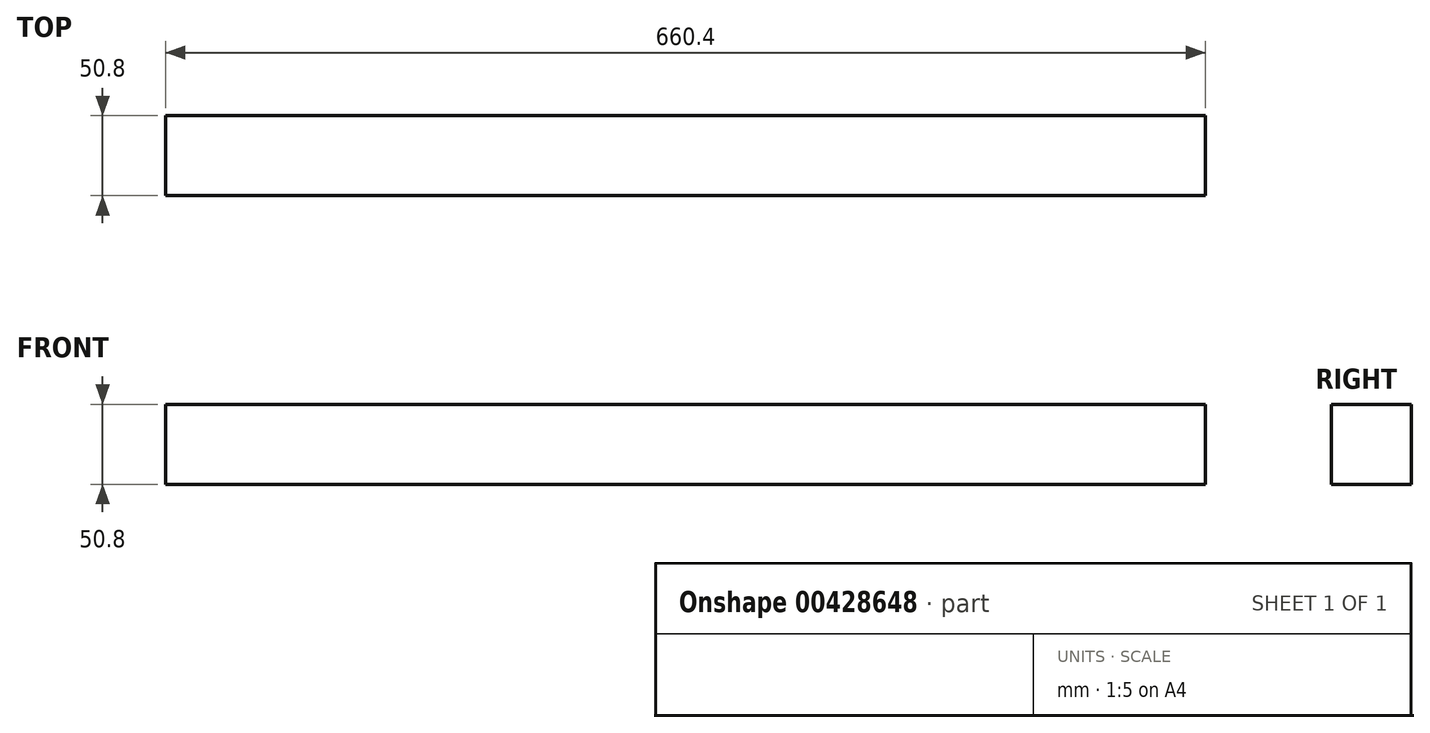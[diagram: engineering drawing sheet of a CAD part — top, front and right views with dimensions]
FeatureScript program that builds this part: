
annotation { "Feature Type Name" : "Feature", "Feature Type Description" : "" }
export const myFeature = defineFeature(function(context is Context, id is Id, definition is map)
    precondition{}
    {
        {
            var Q0;
            Q0=qCreatedBy(makeId("Top.planeOp"),FACE);
            var sketch = newSketch(context, id + "F0", { "sketchPlane" : qUnion([Q0])});
            skLineSegment(sketch, "E0.bottom", {"start": v(-330.2, 25.4) * mm, "end": v(330.2, 25.4) * mm});
            skLineSegment(sketch, "E0.top", {"start": v(-330.2, -25.4) * mm, "end": v(330.2, -25.4) * mm});
            skLineSegment(sketch, "E0.left", {"start": v(-330.2, 25.4) * mm, "end": v(-330.2, -25.4) * mm});
            skLineSegment(sketch, "E0.right", {"start": v(330.2, 25.4) * mm, "end": v(330.2, -25.4) * mm});
            skPoint(sketch, "E0.middle", {"position": v(0, 0) * mm});
            skSolve(sketch);
        }
        {
            var Q0;
            Q0 = qSketchRegion(id + "F0", true);
            extrude(context, id + "F1", {"entities" : qUnion([Q0]), "depth" : 50.8 * mm});
        }
    });
